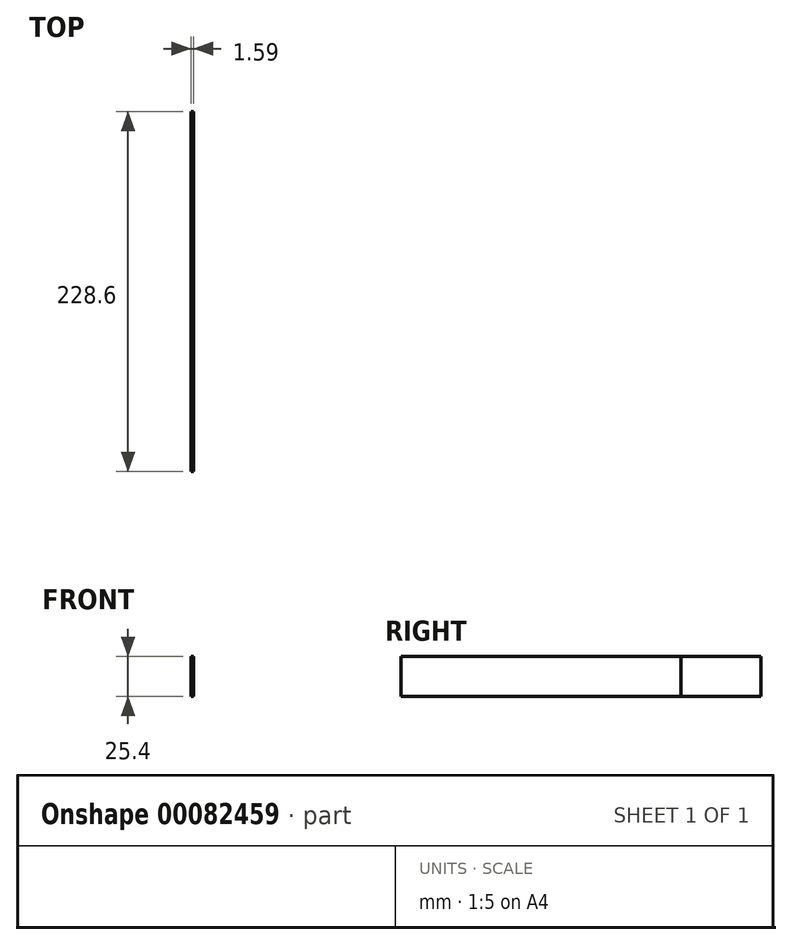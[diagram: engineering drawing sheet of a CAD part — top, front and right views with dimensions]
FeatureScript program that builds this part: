
annotation { "Feature Type Name" : "Feature", "Feature Type Description" : "" }
export const myFeature = defineFeature(function(context is Context, id is Id, definition is map)
    precondition{}
    {
        {
            var Q0;
            Q0=qCreatedBy(makeId("Front.planeOp"),FACE);
            var sketch = newSketch(context, id + "F0", { "sketchPlane" : qUnion([Q0])});
            skLineSegment(sketch, "E0.bottom", {"start": v(0, 0) * mm, "end": v(1.59, 0) * mm});
            skLineSegment(sketch, "E0.top", {"start": v(0, 25.4) * mm, "end": v(1.59, 25.4) * mm});
            skLineSegment(sketch, "E0.left", {"start": v(0, 0) * mm, "end": v(0, 25.4) * mm});
            skLineSegment(sketch, "E0.right", {"start": v(1.59, 0) * mm, "end": v(1.59, 25.4) * mm});
            skSolve(sketch);
        }
        {
            var Q0;
            Q0=qSketchRegion(id+"F0",true);
            extrude(context, id + "F1", {"entities" : qUnion([Q0]), "depth" : 228.6 * mm});
        }
        {
            var Q0;
            Q0 = qSketchRegion(id + "F0", true);
            extrude(context, id + "F2", {"entities" : qUnion([Q0]), "depth" : 50.8 * mm});
        }
    });
